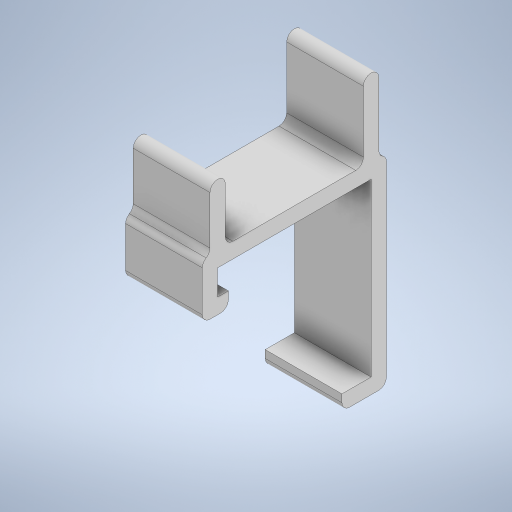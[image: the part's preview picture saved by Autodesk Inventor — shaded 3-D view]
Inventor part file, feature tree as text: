
AUTODESK INVENTOR PART (.ipt)
format: ipt  version: 2023 (Build 270158030, 158C)  size: 294,912 bytes
history: native  units: mm
features: extrude x2, fillet x2, sketch x2
ambient origin geometry x8: Origin, YZ Plane, XZ Plane, XY Plane, X Axis, Y Axis, Z Axis, Center Point
bodies: Solid1 (feature_tree)
feature tree (6):
  extrude  "Extrusion1"  Depth=1.65mm
  fillet  "Fillet1"  Radius=10.0mm
  extrude  "Extrusion2"  Depth=1.0mm
  fillet  "Fillet2"  Radius=1.0mm
  sketch  "Sketch1"  dims[d0=0.7mm d1=1.65mm d2=10.0mm]
  sketch  "Sketch2"  dims[d3=11.165365mm d4=1.0mm d5=1.0mm d6=1.0mm d7=1.0mm d8=1.0mm d9=1.9mm d10=5.0mm d11=0.0mm d12=0.5mm d13=10.0mm d14=1.0mm d15=1.0mm d16=5.0mm d17=4.0mm d18=5.0mm d19=0.0mm d20=0.5mm]
